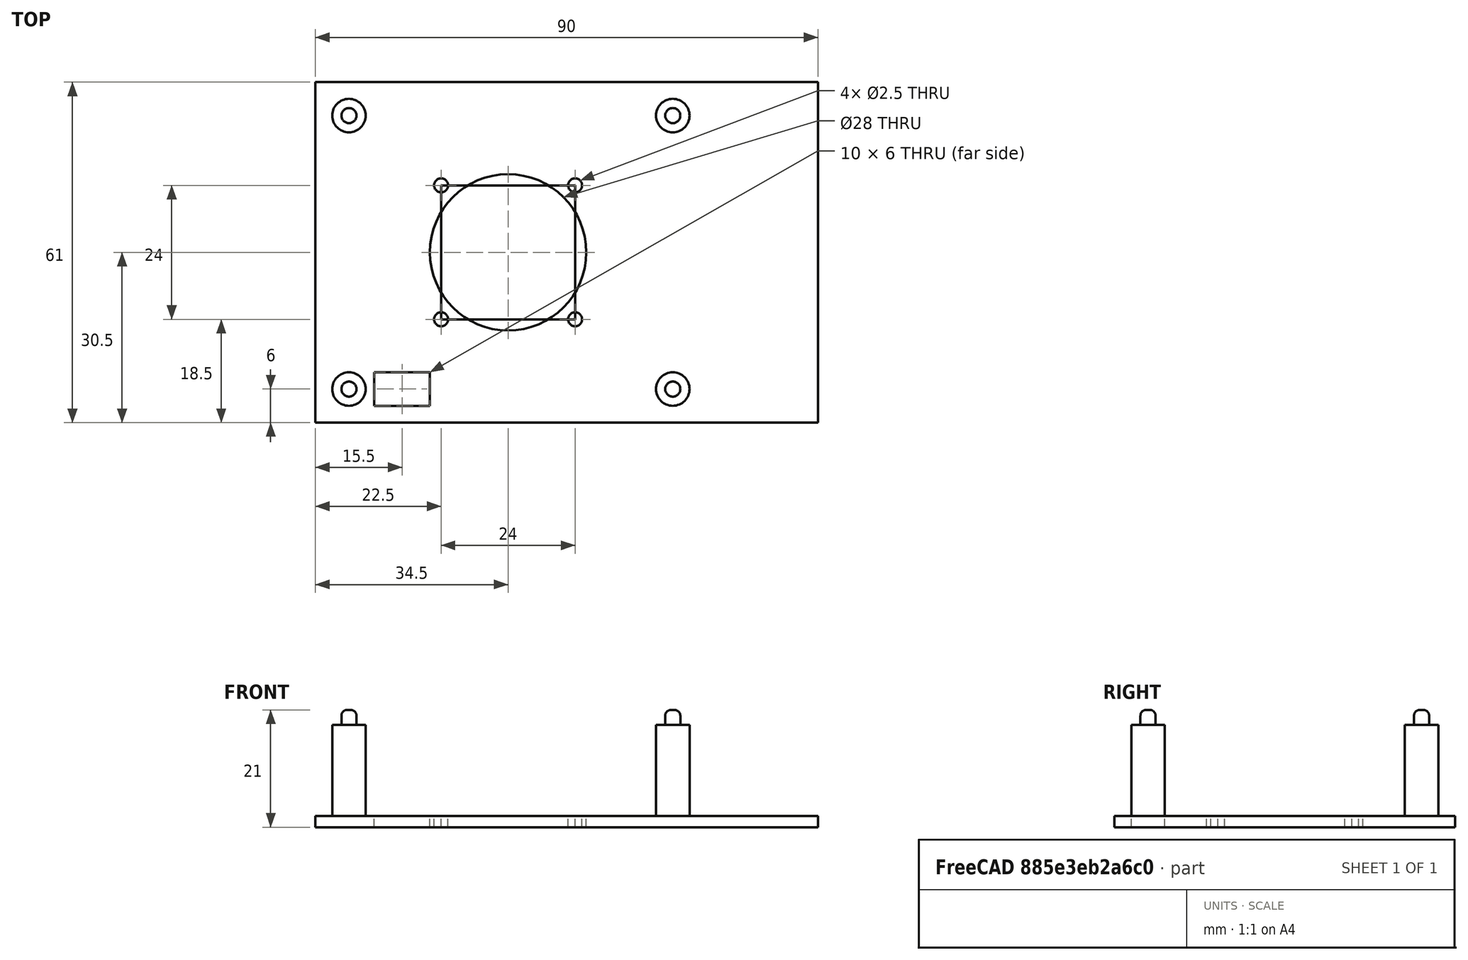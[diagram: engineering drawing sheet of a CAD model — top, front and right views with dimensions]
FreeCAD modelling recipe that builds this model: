
FCSTD DOCUMENT  (FreeCAD 0.18R4 (GitTag))
Label: RPIBaseTop
License: All rights reserved
LicenseURL: http://en.wikipedia.org/wiki/All_rights_reserved
objects: Part::Cylinder×17, Part::Cut×10, Part::Fillet×4, Part::Box×3, Part::MultiFuse×1
note: 35 computed .brp shape members not serialized (recipe doc carries the construction recipe); baked Part::Feature solids carry a one-line shape summary decoded from their .brp

FEATURE [Part::Box] Box  label="Bottom"
  AttacherType = Attacher::AttachEngine3D
  Height = 2
  Length = 90
  Placement = pos=(2.5,2.5,0) rot=(0,0,1;0rad)
  Width = 61
FEATURE [Part::Cylinder] Cylinder  label="Outside Cyl"
  Angle = 360
  AttacherType = Attacher::AttachEngine3D
  Height = 16.3
  Placement = pos=(-8.5,8.5,0) rot=(0,0,1;0rad)
  Radius = 3
FEATURE [Part::Cylinder] Cylinder001  label="Inside Cyl"
  Angle = 360
  AttacherType = Attacher::AttachEngine3D
  Height = 5
  Placement = pos=(-8.5,8.5,0) rot=(0,0,1;0rad)
  Radius = 1
FEATURE [Part::Cylinder] Cylinder002  label="Inside Cyl001"
  Angle = 360
  AttacherType = Attacher::AttachEngine3D
  Height = 5
  Placement = pos=(-8.5,8.5,0) rot=(0,0,1;0rad)
  Radius = 1
FEATURE [Part::Cylinder] Cylinder003  label="Outside Cyl001"
  Angle = 360
  AttacherType = Attacher::AttachEngine3D
  Height = 16.3
  Placement = pos=(-8.5,8.5,0) rot=(0,0,1;0rad)
  Radius = 3
FEATURE [Part::Cut] Cut001  label="Post 02"
  Base = -> Cylinder003
  Placement = pos=(17,49,2) rot=(0,0,1;0rad)
  Tool = -> Cylinder002
FEATURE [Part::Cylinder] Cylinder004  label="Inside Cyl002"
  Angle = 360
  AttacherType = Attacher::AttachEngine3D
  Height = 5
  Placement = pos=(-8.5,8.5,0) rot=(0,0,1;0rad)
  Radius = 1
FEATURE [Part::Cylinder] Cylinder005  label="Outside Cyl002"
  Angle = 360
  AttacherType = Attacher::AttachEngine3D
  Height = 16.3
  Placement = pos=(-8.5,8.5,0) rot=(0,0,1;0rad)
  Radius = 3
FEATURE [Part::Cut] Cut002  label="Post 03"
  Base = -> Cylinder005
  Placement = pos=(75,0,2) rot=(0,0,1;0rad)
  Tool = -> Cylinder004
FEATURE [Part::Cylinder] Cylinder006  label="Inside Cyl003"
  Angle = 360
  AttacherType = Attacher::AttachEngine3D
  Height = 5
  Placement = pos=(-8.5,8.5,0) rot=(0,0,1;0rad)
  Radius = 1
FEATURE [Part::Cylinder] Cylinder007  label="Outside Cyl003"
  Angle = 360
  AttacherType = Attacher::AttachEngine3D
  Height = 16.3
  Placement = pos=(-8.5,8.5,0) rot=(0,0,1;0rad)
  Radius = 3
FEATURE [Part::Cut] Cut003  label="Post 04"
  Base = -> Cylinder007
  Placement = pos=(75,49,2) rot=(0,0,1;0rad)
  Tool = -> Cylinder006
FEATURE [Part::Cut] Cut  label=" Post 01"
  Base = -> Cylinder
  Placement = pos=(17,0,2) rot=(0,0,1;0rad)
  Tool = -> Cylinder001
FEATURE [Part::Cylinder] Cylinder008  label="Pin 001"
  Angle = 360
  AttacherType = Attacher::AttachEngine3D
  Height = 21
  Placement = pos=(8.5,8.5,0) rot=(0,0,1;0rad)
  Radius = 1.35
FEATURE [Part::Fillet] Fillet  label="Pin 002"
  Base = -> Cylinder008
  Edges = 1 edges r=1: [Edge1]
FEATURE [Part::Cylinder] Cylinder009  label="Pin 004"
  Angle = 360
  AttacherType = Attacher::AttachEngine3D
  Height = 21
  Placement = pos=(8.5,8.5,0) rot=(0,0,1;0rad)
  Radius = 1.35
FEATURE [Part::Fillet] Fillet001  label="Pin 003"
  Base = -> Cylinder009
  Edges = 1 edges r=1: [Edge1]
  Placement = pos=(0,49,0) rot=(0,0,1;0rad)
FEATURE [Part::Cylinder] Cylinder010  label="Pin 006"
  Angle = 360
  AttacherType = Attacher::AttachEngine3D
  Height = 21
  Placement = pos=(8.5,8.5,0) rot=(0,0,1;0rad)
  Radius = 1.35
FEATURE [Part::Fillet] Fillet002  label="Pin 005"
  Base = -> Cylinder010
  Edges = 1 edges r=1: [Edge1]
  Placement = pos=(58,0,0) rot=(0,0,1;0rad)
FEATURE [Part::Cylinder] Cylinder011  label="Pin 008"
  Angle = 360
  AttacherType = Attacher::AttachEngine3D
  Height = 21
  Placement = pos=(8.5,8.5,0) rot=(0,0,1;0rad)
  Radius = 1.35
FEATURE [Part::Fillet] Fillet003  label="Pin 007"
  Base = -> Cylinder011
  Edges = 1 edges r=1: [Edge1]
  Placement = pos=(58,49,0) rot=(0,0,1;0rad)
FEATURE [Part::MultiFuse] Fusion  label="Pi Base Top 001"
  Shapes = -> [Box,Cut001,Cut002,Cut003,Cut,Fillet,Fillet001,Fillet002,Fillet003]
FEATURE [Part::Box] Box001  label="Cube"
  AttacherType = Attacher::AttachEngine3D
  Height = 2
  Length = 24
  Placement = pos=(25,21,0) rot=(0,0,1;0rad)
  Width = 24
FEATURE [Part::Cylinder] Cylinder012  label="Mount 001"
  Angle = 360
  AttacherType = Attacher::AttachEngine3D
  Height = 2
  Placement = pos=(25,21,0) rot=(0,0,1;0rad)
  Radius = 1.25
FEATURE [Part::Cylinder] Cylinder013  label="Mount 002"
  Angle = 360
  AttacherType = Attacher::AttachEngine3D
  Height = 2
  Placement = pos=(25,45,0) rot=(0,0,1;0rad)
  Radius = 1.25
FEATURE [Part::Cylinder] Cylinder014  label="Mount 003"
  Angle = 360
  AttacherType = Attacher::AttachEngine3D
  Height = 2
  Placement = pos=(49,45,0) rot=(0,0,1;0rad)
  Radius = 1.25
FEATURE [Part::Cylinder] Cylinder015  label="Mount 004"
  Angle = 360
  AttacherType = Attacher::AttachEngine3D
  Height = 2
  Placement = pos=(49,21,0) rot=(0,0,1;0rad)
  Radius = 1.25
FEATURE [Part::Cylinder] Cylinder016  label="FanHole"
  Angle = 360
  AttacherType = Attacher::AttachEngine3D
  Height = 2
  Placement = pos=(37,33,0) rot=(0,0,1;0rad)
  Radius = 14
FEATURE [Part::Box] Box002  label="Fan Power 001"
  AttacherType = Attacher::AttachEngine3D
  Height = 2
  Length = 10
  Placement = pos=(13,5.5,0) rot=(0,0,1;0rad)
  Width = 6
FEATURE [Part::Cut] Cut004
  Base = -> Fusion
  Tool = -> Cylinder016
FEATURE [Part::Cut] Cut005
  Base = -> Cut004
  Tool = -> Box002
FEATURE [Part::Cut] Cut006
  Base = -> Cut005
  Tool = -> Cylinder015
FEATURE [Part::Cut] Cut007
  Base = -> Cut006
  Tool = -> Cylinder014
FEATURE [Part::Cut] Cut008
  Base = -> Cut007
  Tool = -> Cylinder013
FEATURE [Part::Cut] Cut009  label="RPi Base Top"
  Base = -> Cut008
  Tool = -> Cylinder012
